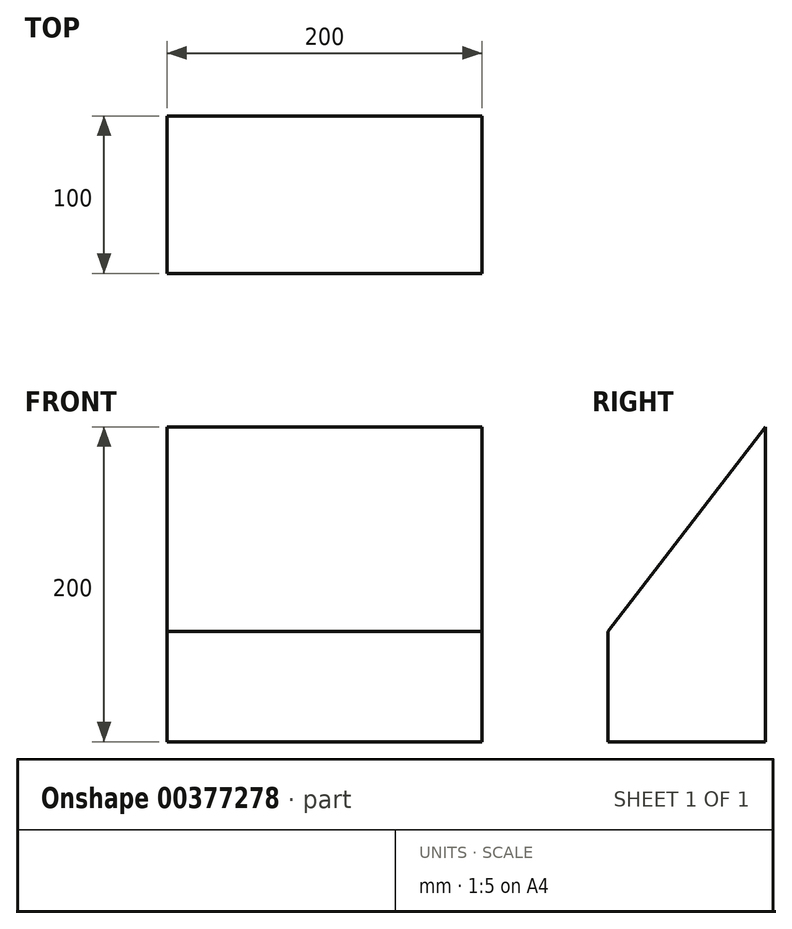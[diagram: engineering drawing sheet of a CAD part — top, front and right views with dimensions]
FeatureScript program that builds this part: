
annotation { "Feature Type Name" : "Feature", "Feature Type Description" : "" }
export const myFeature = defineFeature(function(context is Context, id is Id, definition is map)
    precondition{}
    {
        {
            var Q0;
            Q0=qCreatedBy(makeId("Top.planeOp"),FACE);
            var sketch = newSketch(context, id + "F0", { "sketchPlane" : qUnion([Q0])});
            skLineSegment(sketch, "E0.bottom", {"start": v(100, -50) * mm, "end": v(-100, -50) * mm});
            skLineSegment(sketch, "E0.top", {"start": v(100, 50) * mm, "end": v(-100, 50) * mm});
            skLineSegment(sketch, "E0.left", {"start": v(100, -50) * mm, "end": v(100, 50) * mm});
            skLineSegment(sketch, "E0.right", {"start": v(-100, -50) * mm, "end": v(-100, 50) * mm});
            skPoint(sketch, "E0.middle", {"position": v(0, 0) * mm});
            skSolve(sketch);
        }
        {
            var Q0;
            Q0=makeQuery(id+"F0.imprint","IMPRINT",FACE,{"disambiguationData":[TD([[makeQuery(id+"F0.imprint","IMPRINT",EDGE,{"derivedFrom":sQuery(id+"F0.wireOp",EDGE,"E0.bottom")}),-1.0]])]});
            extrude(context, id + "F1", {"entities" : qUnion([Q0]), "depth" : 5 * mm});
        }
        {
            var Q0;
            Q0=makeQuery(id+"F1.opExtrude","SWEPT_FACE",FACE,{"disambiguationData":[OSD([sQuery(id+"F0.wireOp",EDGE,"E0.left")])]});
            var sketch = newSketch(context, id + "F2", { "sketchPlane" : qUnion([Q0])});
            skLineSegment(sketch, "E1", {"start": v(-50, 0) * mm, "end": v(50, 0) * mm});
            skLineSegment(sketch, "E2", {"start": v(50, 0) * mm, "end": v(50, 200) * mm});
            skLineSegment(sketch, "E3", {"start": v(-50, 0) * mm, "end": v(-50, 70) * mm});
            skLineSegment(sketch, "E4", {"start": v(50, 200) * mm, "end": v(-50, 70) * mm});
            skSolve(sketch);
        }
        {
            var Q0;
            {var subQ2=sQuery(id+"F2.wireOp",EDGE,"E4");Q0=makeQuery(id+"F2.imprint","IMPRINT",FACE,{"disambiguationData":[TD([[makeQuery(id+"F2.imprint","IMPRINT",EDGE,{"derivedFrom":subQ2}),1.0]])]});}
            extrude(context, id + "F3", {"entities" : qUnion([Q0]), "operationType" : NewBodyOperationType.ADD, "oppositeDirection" : true, "depth" : 200 * mm});
        }
    });
